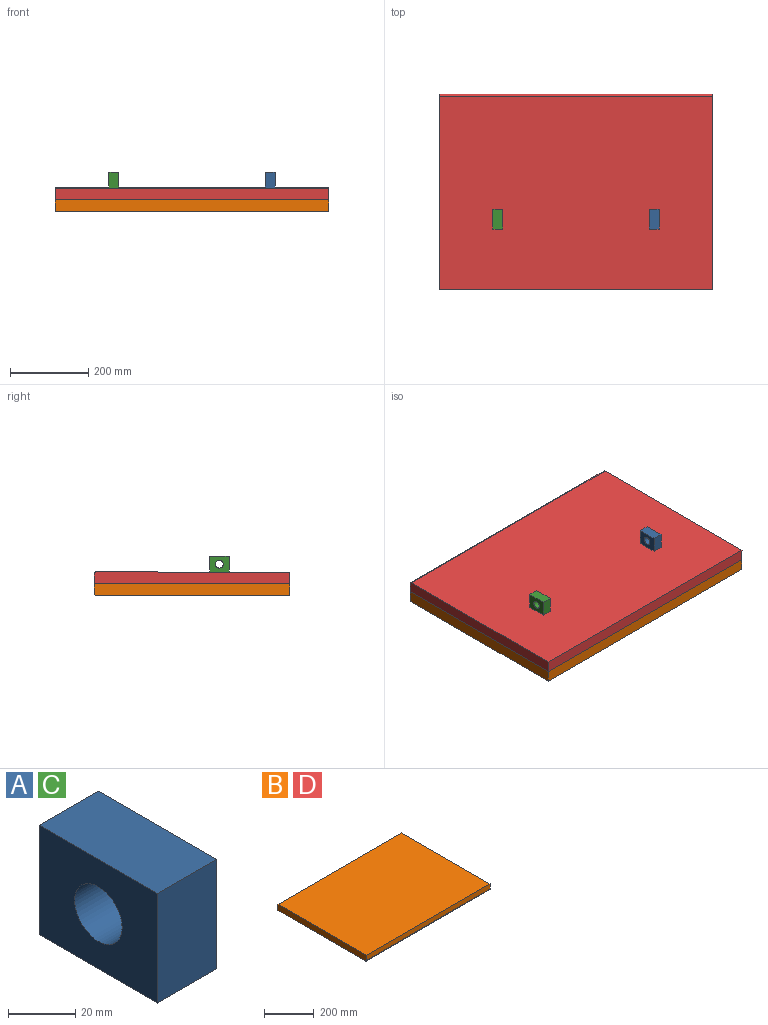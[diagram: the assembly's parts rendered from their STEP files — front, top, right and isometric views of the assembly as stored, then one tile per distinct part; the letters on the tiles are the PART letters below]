
ASSEMBLY  parts=4 mates=3
PART A: 7 faces, bbox 25x50x40 mm
  f0: plane 50x25mm, normal (0,0,1), area 1250mm2, adj f1,f4,f5,f6
  f1: plane 40x25mm, normal (0,1,0), area 1000mm2, adj f0,f2,f5,f6
  f2: plane 50x25mm, normal (0,0,-1), area 1250mm2, adj f1,f4,f5,f6
  f3: cylinder r=10mm len=25mm, axis (1,0,0), area 1570.8mm2, adj f5,f6
  f4: plane 40x25mm, normal (0,-1,0), area 1000mm2, adj f0,f2,f5,f6
  f5: plane 50x40mm, normal (-1,0,0), area 1685.8mm2, adj f0,f1,f2,f3,f4
  f6: plane 50x40mm, normal (1,0,0), area 1685.8mm2, adj f0,f1,f2,f3,f4
PART B: 7 faces, bbox 700x500x30 mm
  f0: plane 700x30mm, normal (0,1,0), area 21000mm2, adj f1,f3,f4,f5
  f1: plane 500x30mm, normal (-1,0,0), area 14994.6mm2, adj f0,f2,f4,f5,f6
  f2: plane 700x25mm, normal (0,-1,0), area 17500mm2, adj f1,f3,f4,f6
  f3: plane 500x30mm, normal (1,0,0), area 14994.6mm2, adj f0,f2,f4,f5,f6
  f4: plane 700x500mm, normal (0,0,1), area 350000mm2, adj f0,f1,f2,f3
  f5: plane 700x495mm, normal (0,0,-1), area 346500mm2, adj f0,f1,f3,f6
  f6: cylinder r=5mm len=700mm, axis (1,0,0), area 5497.8mm2, adj f1,f2,f3,f5
PART C: same geometry as A
PART D: same geometry as B
PLACE A rot(axis=(-1,0,0),179.9deg) t=(762.91,-266.94,59.36)mm
PLACE B rot(axis=(0,0,1),180deg) t=(0.41,-266.88,-0.64)mm fixed
PLACE C rot(axis=(-1,0,0),179.9deg) t=(362.91,-266.94,59.36)mm
PLACE D rot(axis=(-1,0,0),179.9deg) t=(-699.59,-266.94,59.36)mm
MATE fastened A.f0 <-> D.f5  axis (0,0,-1) through (-149.59,-86.68,59.53)mm
MATE fastened C.f0 <-> D.f5  axis (0,0,-1) through (-549.59,-86.68,59.53)mm
MATE revolute D.f1 <-> B.f3  axis (-1,0,0) through (-699.59,-266.91,29.36)mm
